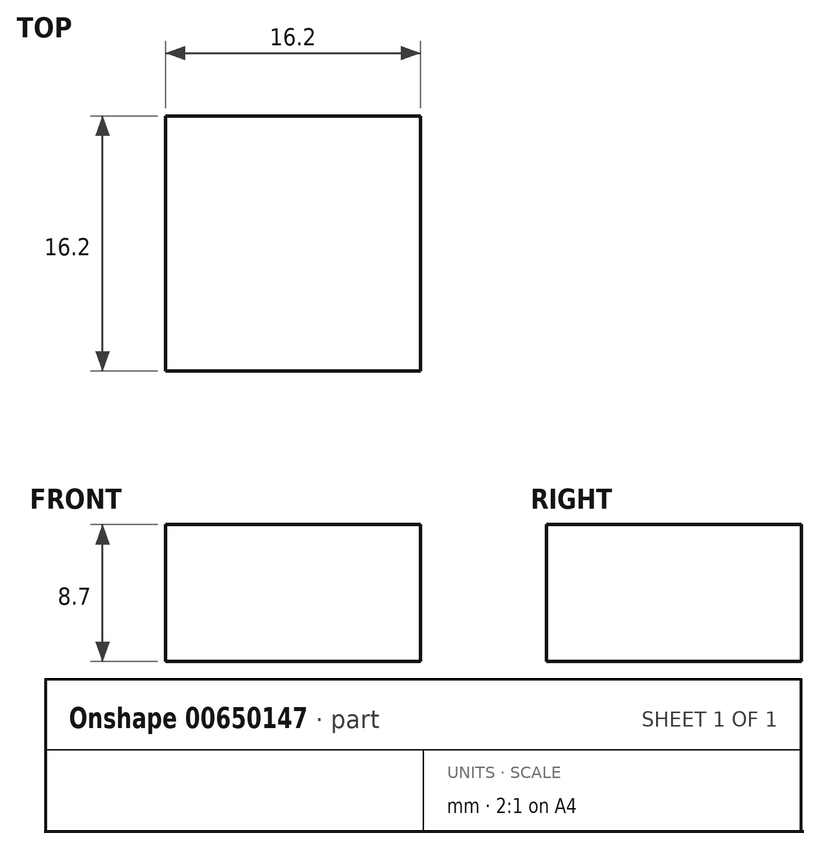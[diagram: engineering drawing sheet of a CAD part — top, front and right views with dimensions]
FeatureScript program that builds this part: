
annotation { "Feature Type Name" : "Feature", "Feature Type Description" : "" }
export const myFeature = defineFeature(function(context is Context, id is Id, definition is map)
    precondition{}
    {
        {
            var Q0;
            Q0=qCreatedBy(makeId("Top.planeOp"),FACE);
            var sketch = newSketch(context, id + "F0", { "sketchPlane" : qUnion([Q0])});
            skLineSegment(sketch, "E0.bottom", {"start": v(10.45, 0) * mm, "end": v(-5.75, 0) * mm});
            skLineSegment(sketch, "E0.top", {"start": v(10.45, -16.2) * mm, "end": v(-5.75, -16.2) * mm});
            skLineSegment(sketch, "E0.left", {"start": v(10.45, 0) * mm, "end": v(10.45, -16.2) * mm});
            skLineSegment(sketch, "E0.right", {"start": v(-5.75, 0) * mm, "end": v(-5.75, -16.2) * mm});
            skSolve(sketch);
        }
        {
            var Q0;
            Q0=makeQuery(id+"F0.imprint","IMPRINT",FACE,{"disambiguationData":[TD([[makeQuery(id+"F0.imprint","IMPRINT",EDGE,{"derivedFrom":sQuery(id+"F0.wireOp",EDGE,"E0.bottom")}),1.0]])]});
            extrude(context, id + "F1", {"entities" : qUnion([Q0]), "depth" : 8.7 * mm, "offsetDistance" : 25 * mm});
        }
    });
